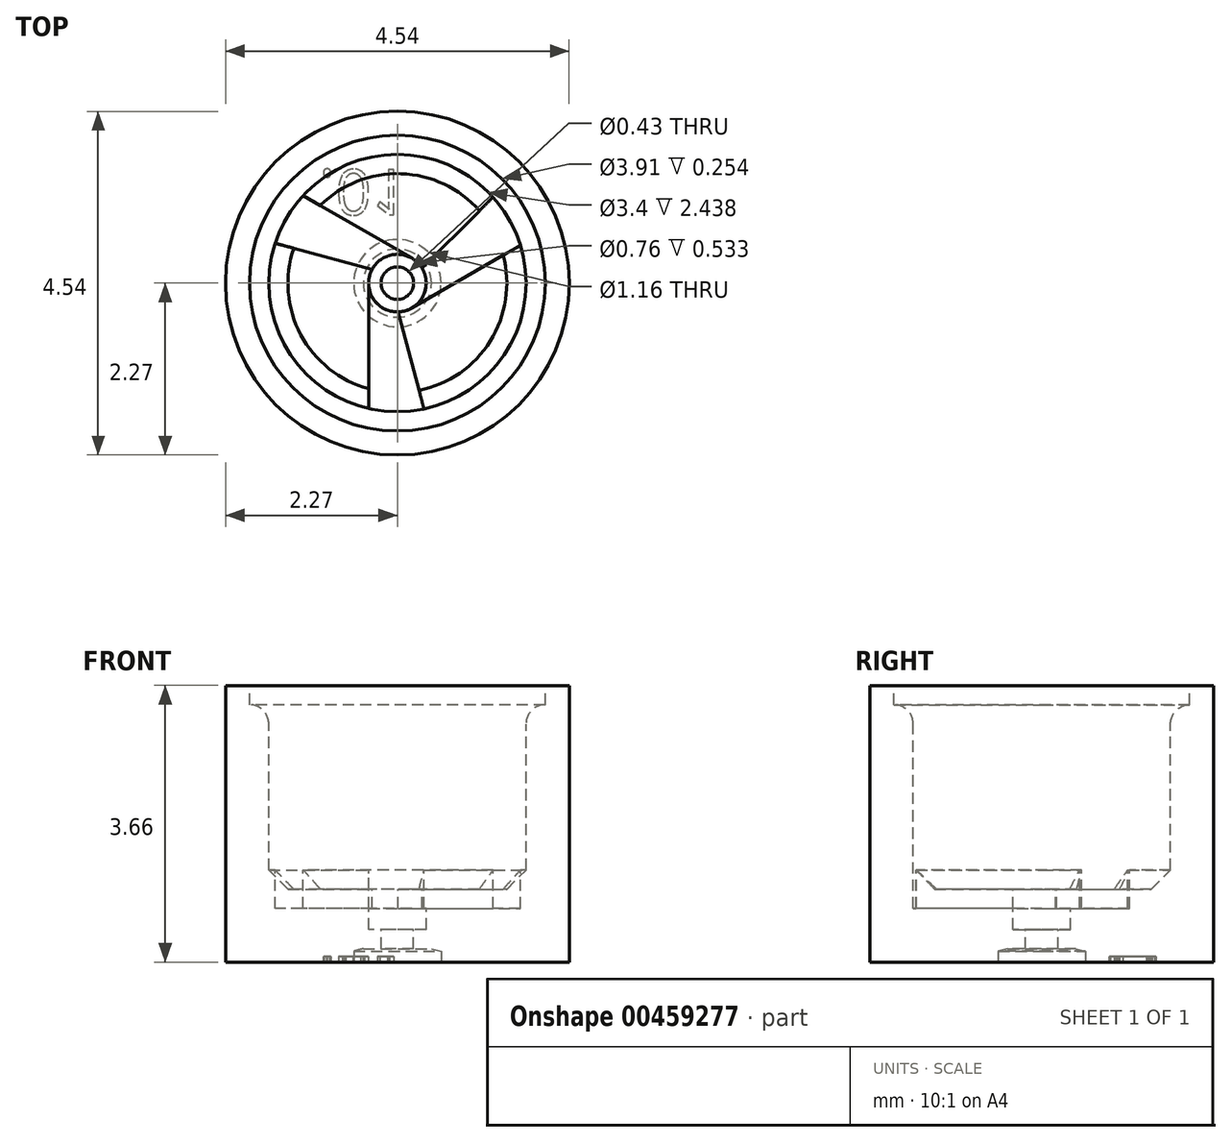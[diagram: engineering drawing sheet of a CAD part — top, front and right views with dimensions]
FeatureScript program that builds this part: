
annotation { "Feature Type Name" : "Feature", "Feature Type Description" : "" }
export const myFeature = defineFeature(function(context is Context, id is Id, definition is map)
    precondition{}
    {
        {
            var Q0;
            Q0=qCreatedBy(makeId("Top.planeOp"),FACE);
            var sketch = newSketch(context, id + "F0", { "sketchPlane" : qUnion([Q0])});
            skCircle(sketch, "E0", {"center": v(0, 0) * mm, "radius": 2.27 * mm});
            skSolve(sketch);
        }
        {
            var Q0;
            Q0=qSketchRegion(id+"F0",true);
            extrude(context, id + "F1", {"entities" : qUnion([Q0]), "depth" : 3.66 * mm});
        }
        {
            var Q0;
            Q0=makeQuery(id+"F1.opExtrude","CAP_FACE",FACE,{"disambiguationData":[OSD([sQuery(id+"F0.wireOp",EDGE,"E0")])],"isStart":false});
            var sketch = newSketch(context, id + "F2", { "sketchPlane" : qUnion([Q0])});
            skCircle(sketch, "E1", {"center": v(0, 0) * mm, "radius": 1.96 * mm});
            skSolve(sketch);
        }
        {
            var Q0;
            Q0=makeQuery(id+"F2.imprint","IMPRINT",FACE,{"disambiguationData":[TD([[makeQuery(id+"F2.imprint","IMPRINT",EDGE,{"derivedFrom":sQuery(id+"F2.wireOp",EDGE,"E1")}),1.0]])]});
            extrude(context, id + "F3", {"entities" : qUnion([Q0]), "operationType" : NewBodyOperationType.REMOVE, "oppositeDirection" : true, "depth" : 0.25 * mm});
        }
        {
            var Q0;
            Q0=makeQuery(id+"F3.boolean.opBoolean","COPY",FACE,{"derivedFrom":makeQuery(id+"F3.opExtrude","CAP_FACE",FACE,{"disambiguationData":[OSD([sQuery(id+"F2.wireOp",EDGE,"E1")])],"isStart":false})});
            var sketch = newSketch(context, id + "F4", { "sketchPlane" : qUnion([Q0])});
            skCircle(sketch, "E2", {"center": v(0, 0) * mm, "radius": 1.7 * mm});
            skSolve(sketch);
        }
        {
            var Q0;
            Q0=makeQuery(id+"F4.imprint","IMPRINT",FACE,{"disambiguationData":[TD([[makeQuery(id+"F4.imprint","IMPRINT",EDGE,{"derivedFrom":sQuery(id+"F4.wireOp",EDGE,"E2")}),1.0]])]});
            extrude(context, id + "F5", {"entities" : qUnion([Q0]), "operationType" : NewBodyOperationType.REMOVE, "oppositeDirection" : true, "depth" : 2.44 * mm});
        }
        {
            var Q0;
            Q0=makeQuery(id+"F5.boolean.opBoolean","COPY",EDGE,{"derivedFrom":makeQuery(id+"F5.opExtrude","CAP_EDGE",EDGE,{"disambiguationData":[OSD([sQuery(id+"F4.wireOp",EDGE,"E2")])],"isStart":false})});
            chamfer(context, id + "F6", {"entities" : qUnion([Q0]), "chamferType" : ChamferType.OFFSET_ANGLE, "width" : 0.25 * mm, "oppositeDirection" : false, "angle" : 45 * degree, "tangentPropagation" : true});
        }
        {
            var Q0;
            Q0=makeQuery(id+"F5.boolean.opBoolean","COPY",FACE,{"derivedFrom":makeQuery(id+"F5.opExtrude","CAP_FACE",FACE,{"disambiguationData":[OSD([sQuery(id+"F4.wireOp",EDGE,"E2")])],"isStart":false})});
            var sketch = newSketch(context, id + "F7", { "sketchPlane" : qUnion([Q0])});
            skCircle(sketch, "E3", {"center": v(0, 0) * mm, "radius": 0.38 * mm});
            skSolve(sketch);
        }
        {
            var Q0;
            Q0=makeQuery(id+"F7.imprint","IMPRINT",FACE,{"disambiguationData":[TD([[makeQuery(id+"F7.imprint","IMPRINT",EDGE,{"derivedFrom":sQuery(id+"F7.wireOp",EDGE,"E3")}),1.0]])]});
            extrude(context, id + "F8", {"entities" : qUnion([Q0]), "operationType" : NewBodyOperationType.REMOVE, "oppositeDirection" : true, "depth" : 0.53 * mm});
        }
        {
            var Q0;
            Q0=makeQuery(id+"F8.boolean.opBoolean","COPY",FACE,{"derivedFrom":makeQuery(id+"F8.opExtrude","CAP_FACE",FACE,{"disambiguationData":[OSD([sQuery(id+"F7.wireOp",EDGE,"E3")])],"isStart":false})});
            var sketch = newSketch(context, id + "F9", { "sketchPlane" : qUnion([Q0])});
            skCircle(sketch, "E4", {"center": v(0, 0) * mm, "radius": 0.21 * mm});
            skSolve(sketch);
        }
        {
            var Q0;
            Q0=makeQuery(id+"F9.imprint","IMPRINT",FACE,{"disambiguationData":[TD([[makeQuery(id+"F9.imprint","IMPRINT",EDGE,{"derivedFrom":sQuery(id+"F9.wireOp",EDGE,"E4")}),1.0]])]});
            extrude(context, id + "F10", {"entities" : qUnion([Q0]), "operationType" : NewBodyOperationType.REMOVE, "oppositeDirection" : true, "depth" : 25.4 * mm});
        }
        {
            var Q0;
            Q0=makeQuery(id+"F1.opExtrude","CAP_FACE",FACE,{"disambiguationData":[OSD([sQuery(id+"F0.wireOp",EDGE,"E0")])],"isStart":true});
            var sketch = newSketch(context, id + "F11", { "sketchPlane" : qUnion([Q0])});
            skCircle(sketch, "E5", {"center": v(0, 0) * mm, "radius": 0.58 * mm});
            skSolve(sketch);
        }
        {
            var Q0;
            Q0=makeQuery(id+"F11.imprint","IMPRINT",FACE,{"disambiguationData":[TD([[makeQuery(id+"F11.imprint","IMPRINT",EDGE,{"derivedFrom":sQuery(id+"F11.wireOp",EDGE,"E5")}),1.0]])]});
            extrude(context, id + "F12", {"entities" : qUnion([Q0]), "operationType" : NewBodyOperationType.REMOVE, "oppositeDirection" : true, "depth" : 0.18 * mm});
        }
        {
            var Q0;
            Q0=makeQuery(id+"F12.boolean.opBoolean","COPY",EDGE,{"derivedFrom":makeQuery(id+"F12.opExtrude","CAP_EDGE",EDGE,{"disambiguationData":[OSD([sQuery(id+"F11.wireOp",EDGE,"E5")])],"isStart":false})});
            chamfer(context, id + "F13", {"entities" : qUnion([Q0]), "chamferType" : ChamferType.OFFSET_ANGLE, "width" : 0.13 * mm, "oppositeDirection" : false, "angle" : 15 * degree, "tangentPropagation" : true});
        }
        {
            var Q0;
            Q0=makeQuery(id+"F5.boolean.opBoolean","COPY",FACE,{"derivedFrom":makeQuery(id+"F5.opExtrude","CAP_FACE",FACE,{"disambiguationData":[OSD([sQuery(id+"F4.wireOp",EDGE,"E2")])],"isStart":false})});
            var sketch = newSketch(context, id + "F14", { "sketchPlane" : qUnion([Q0])});
            skArc(sketch, "E6.0", {"start": v(0.2, 0.33) * mm, "mid": v(-0.1, 0.37) * mm, "end": v(-0.33, 0.18) * mm});
            skArc(sketch, "E7.0", {"start": v(-1.25, 1.16) * mm, "mid": v(-1.47, 0.86) * mm, "end": v(-1.62, 0.53) * mm});
            skLineSegment(sketch, "E8", {"start": v(0.2, 0.33) * mm, "end": v(-1.25, 1.16) * mm});
            skLineSegment(sketch, "E9", {"start": v(-0.33, 0.18) * mm, "end": v(-1.62, 0.53) * mm});
            skLineSegment(sketch, "E10.1.0", {"start": v(-0.38, 0) * mm, "end": v(-0.38, -1.66) * mm});
            skArc(sketch, "E10.1.1", {"start": v(-0.38, 0) * mm, "mid": v(-0.27, -0.27) * mm, "end": v(0, -0.38) * mm});
            skLineSegment(sketch, "E10.1.2", {"start": v(0, -0.38) * mm, "end": v(0.35, -1.66) * mm});
            skArc(sketch, "E10.1.3", {"start": v(-0.38, -1.66) * mm, "mid": v(-0.01, -1.7) * mm, "end": v(0.35, -1.66) * mm});
            skLineSegment(sketch, "E10.2.0", {"start": v(0.2, -0.33) * mm, "end": v(1.63, 0.5) * mm});
            skArc(sketch, "E10.2.1", {"start": v(0.2, -0.33) * mm, "mid": v(0.37, -0.1) * mm, "end": v(0.33, 0.2) * mm});
            skLineSegment(sketch, "E10.2.2", {"start": v(0.33, 0.2) * mm, "end": v(1.27, 1.14) * mm});
            skArc(sketch, "E10.2.3", {"start": v(1.63, 0.5) * mm, "mid": v(1.48, 0.84) * mm, "end": v(1.27, 1.14) * mm});
            skSolve(sketch);
        }
        {
            var Q0;
            Q0=qSketchRegion(id+"F14",true);
            extrude(context, id + "F15", {"entities" : qUnion([Q0]), "operationType" : NewBodyOperationType.REMOVE, "oppositeDirection" : true, "depth" : 0.25 * mm});
        }
        {
            var Q0;
            Q0=qSketchRegion(id+"F14",true);
            extrude(context, id + "F16", {"entities" : qUnion([Q0]), "operationType" : NewBodyOperationType.REMOVE, "depth" : 25.4 * mm});
        }
        {
            var Q0;
            Q0=makeQuery(id+"F16.boolean.opBoolean","INTERSECT",EDGE,{"derivedFrom":[makeQuery(id+"F16.opExtrude","SWEPT_FACE",FACE,{"disambiguationData":[OSD([sQuery(id+"F14.wireOp",EDGE,"E7.0")])]}),makeQuery(id+"F16.opExtrude","SWEPT_FACE",FACE,{"disambiguationData":[OSD([sQuery(id+"F14.wireOp",EDGE,"E10.1.3")])]}),makeQuery(id+"F16.opExtrude","SWEPT_FACE",FACE,{"disambiguationData":[OSD([sQuery(id+"F14.wireOp",EDGE,"E10.2.3")])]})]});
            fillet(context, id + "F17", {"entities" : qUnion([Q0]), "radius" : 0.25 * mm, "tangentPropagation" : true, "allowEdgeOverflow" : false});
        }
        {
            var Q0;
            Q0=makeQuery(id+"F1.opExtrude","CAP_FACE",FACE,{"disambiguationData":[OSD([sQuery(id+"F0.wireOp",EDGE,"E0")])],"isStart":true});
            var sketch = newSketch(context, id + "F18", { "sketchPlane" : qUnion([Q0])});
            skText(sketch, "E11", { "text": ".01\n", "fontName": "OpenSans-Regular.ttf"});
            const initialGuessF18  = {"E11": [-0.00104, -0.0015, 1, 0, 0.0006]};
            skSetInitialGuess(sketch, initialGuessF18);
            skSolve(sketch);
        }
        {
            var Q0;
            Q0 = qSketchRegion(id + "F18", true);
            extrude(context, id + "F19", {"entities" : qUnion([Q0]), "operationType" : NewBodyOperationType.REMOVE, "oppositeDirection" : true, "depth" : 0.08 * mm});
        }
    });
